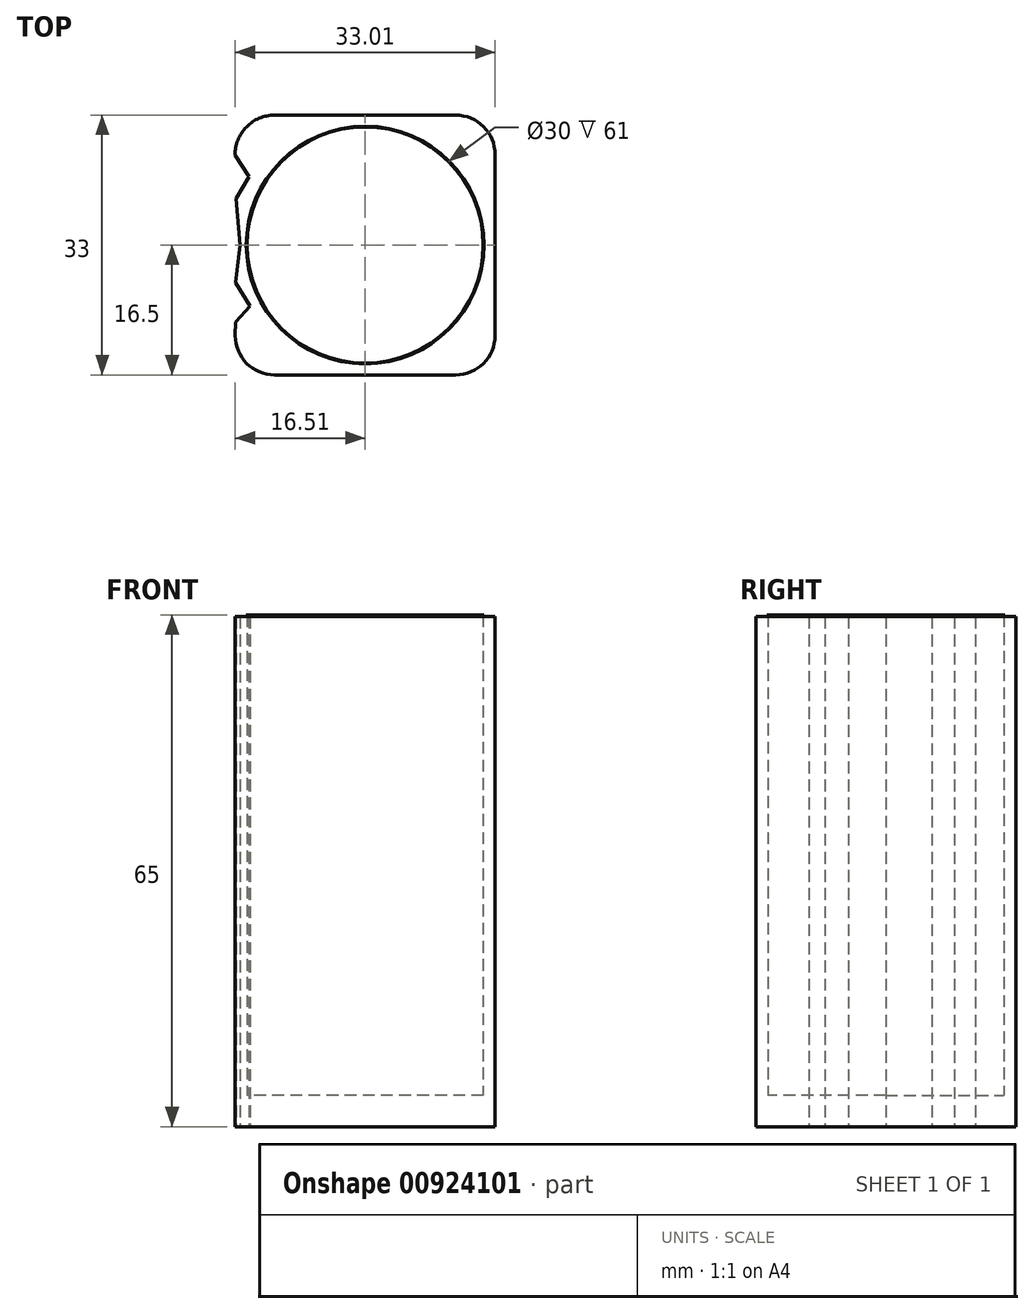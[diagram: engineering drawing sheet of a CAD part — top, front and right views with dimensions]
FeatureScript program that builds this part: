
annotation { "Feature Type Name" : "Feature", "Feature Type Description" : "" }
export const myFeature = defineFeature(function(context is Context, id is Id, definition is map)
    precondition{}
    {
        {
            var Q0;
            Q0=qCreatedBy(makeId("Front.planeOp"),FACE);
            var sketch = newSketch(context, id + "F0", { "sketchPlane" : qUnion([Q0])});
            skLineSegment(sketch, "E0", {"start": v(0, 0) * mm, "end": v(0, 26.34) * mm});
            skLineSegment(sketch, "E1", {"start": v(-15, 0) * mm, "end": v(-15, 65) * mm});
            skLineSegment(sketch, "E2", {"start": v(-15, 65) * mm, "end": v(-15.1, 65) * mm});
            skLineSegment(sketch, "E3", {"start": v(-15.1, 65) * mm, "end": v(-15.1, 0) * mm});
            skLineSegment(sketch, "E4", {"start": v(-15.1, 0) * mm, "end": v(-15, 0) * mm});
            skSolve(sketch);
        }
        {
            var Q0;
            Q0=makeQuery(id+"F0.imprint","IMPRINT",FACE,{"disambiguationData":[TD([[makeQuery(id+"F0.imprint","IMPRINT",EDGE,{"derivedFrom":sQuery(id+"F0.wireOp",EDGE,"E1")}),1.0]])]});
            var Q1;
            Q1=sQuery(id+"F0.wireOp",EDGE,"E0");
            revolve(context, id + "F1", {"surfaceOperationType" : NewSurfaceOperationType.NEW, "entities" : qUnion([Q0]), "axis" : qUnion([Q1]), "revolveType" : RevolveType.FULL});
        }
        {
            var Q0;
            Q0=qCreatedBy(makeId("Top.planeOp"),FACE);
            var sketch = newSketch(context, id + "F2", { "sketchPlane" : qUnion([Q0])});
            skLineSegment(sketch, "E5.bottom", {"start": v(11.5, -16.5) * mm, "end": v(-11.5, -16.5) * mm});
            skLineSegment(sketch, "E5.top", {"start": v(11.5, 16.5) * mm, "end": v(-11.5, 16.5) * mm});
            skLineSegment(sketch, "E5.left", {"start": v(16.5, -11.5) * mm, "end": v(16.5, 11.5) * mm});
            skPoint(sketch, "E5.middle", {"position": v(0, 0) * mm});
            skPoint(sketch, "E6.visualSharp", {"position": v(16.5, -16.5) * mm});
            skArc(sketch, "E6.filletArc", {"start": v(11.5, -16.5) * mm, "mid": v(15.04, -15.04) * mm, "end": v(16.5, -11.5) * mm});
            skPoint(sketch, "E7.visualSharp", {"position": v(-16.5, -16.5) * mm});
            skArc(sketch, "E7.filletArc", {"start": v(-16.5, -11.5) * mm, "mid": v(-15.04, -15.04) * mm, "end": v(-11.5, -16.5) * mm});
            skPoint(sketch, "E8.visualSharp", {"position": v(-16.5, 16.5) * mm});
            skArc(sketch, "E8.filletArc", {"start": v(-11.5, 16.5) * mm, "mid": v(-15.08, 15) * mm, "end": v(-16.5, 11.4) * mm});
            skPoint(sketch, "E9.visualSharp", {"position": v(16.5, 16.5) * mm});
            skArc(sketch, "E9.filletArc", {"start": v(16.5, 11.5) * mm, "mid": v(15.04, 15.04) * mm, "end": v(11.5, 16.5) * mm});
            skCircle(sketch, "E10", {"center": v(0, 0) * mm, "radius": 15.1 * mm});
            skLineSegment(sketch, "E11", {"start": v(-14.72, 8.7) * mm, "end": v(-16.42, 5.87) * mm});
            skLineSegment(sketch, "E12", {"start": v(-16.42, 5.87) * mm, "end": v(-15.87, 0) * mm});
            skLineSegment(sketch, "E13", {"start": v(-15.87, 0) * mm, "end": v(-16.47, -4.76) * mm});
            skLineSegment(sketch, "E14", {"start": v(-16.47, -4.76) * mm, "end": v(-14.64, -7.76) * mm});
            skLineSegment(sketch, "E15", {"start": v(-14.64, -7.76) * mm, "end": v(-16.5, -9.78) * mm});
            skLineSegment(sketch, "E16", {"start": v(-16.5, -9.78) * mm, "end": v(-16.5, -11.5) * mm});
            skPoint(sketch, "E17", {"position": v(-16.42, 8.7) * mm});
            skPoint(sketch, "E18.end.orphan", {"position": v(-16.5, 11.4) * mm});
            skLineSegment(sketch, "E19", {"start": v(-14.72, 8.7) * mm, "end": v(-16.5, 11.4) * mm});
            skLineSegment(sketch, "E20", {"start": v(14.05, 8.7) * mm, "end": v(16.5, 11.5) * mm});
            skSolve(sketch);
        }
        {
            var Q0;
            Q0=makeQuery(id+"F2.imprint","IMPRINT",FACE,{"disambiguationData":[TD([[makeQuery(id+"F2.imprint","IMPRINT",EDGE,{"derivedFrom":sQuery(id+"F2.wireOp",EDGE,"E5.bottom")}),-1.0]])]});
            extrude(context, id + "F3", {"entities" : qUnion([Q0]), "operationType" : NewBodyOperationType.ADD, "depth" : 64.8 * mm, "offsetDistance" : 25 * mm});
        }
        {
            var Q0;
            Q0=qCreatedBy(makeId("Top.planeOp"),FACE);
            var sketch = newSketch(context, id + "F4", { "sketchPlane" : qUnion([Q0])});
            skCircle(sketch, "E21", {"center": v(0, 0) * mm, "radius": 15.09 * mm});
            skSolve(sketch);
        }
        {
            var Q0;
            Q0 = qSketchRegion(id + "F4", true);
            extrude(context, id + "F5", {"entities" : qUnion([Q0]), "operationType" : NewBodyOperationType.ADD, "depth" : 4 * mm, "offsetDistance" : 25 * mm});
        }
    });
